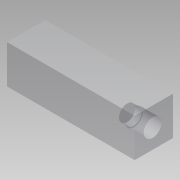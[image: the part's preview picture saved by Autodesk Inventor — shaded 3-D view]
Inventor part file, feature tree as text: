
AUTODESK INVENTOR PART (.ipt)
format: ipt  version: 2014 (Build 180170000, 170)  size: 129,024 bytes
history: native  units: mm
features: other x48, extrude x4, sketch x4
ambient origin geometry x8: Origin, YZ Plane, XZ Plane, XY Plane, X Axis, Y Axis, Z Axis, Center Point
bodies: 实体1 (feature_tree)
feature tree (56):
  extrude  "拉伸1"  Depth=20.0mm
  other  "UCS1"
  other  "UCS2"
  other  "UCS3"
  other  "UCS4"
  other  "UCS5"
  other  "UCS6"
  extrude  "拉伸2"  Depth=20.0mm
  extrude  "拉伸3"  Depth=20.0mm
  extrude  "拉伸4"  Depth=20.0mm TaperAngle=0.0deg
  sketch  "草图1"  dims[d0=30.0mm d1=0.0mm]
  sketch  "草图2"  dims[d2=0.0mm d3=0.0mm d4=0.0mm d5=0.0mm d6=0.0mm d7=0.0mm]
  sketch  "草图3"  dims[d8=0.0mm d9=0.0mm d10=0.0mm d11=0.0mm d12=0.0mm d13=0.0mm]
  sketch  "草图4"  dims[d14=0.0mm d15=0.0mm d16=0.0mm d17=0.0mm d18=0.0mm d19=0.0mm d20=0.0mm d21=0.0mm d22=0.0mm d23=0.0mm d24=0.0mm d25=0.0mm d26=0.0mm d27=0.0mm d28=0.0mm d29=0.0mm d30=0.0mm d31=0.0mm d32=0.0mm d33=0.0mm d34=0.0mm d35=0.0mm d36=0.0mm d37=0.0mm d38=14.0mm d39=15.0mm d40=14.0mm d41=14.5mm d42=0.0mm d43=14.5mm d44=-10.471976mm d45=12.7mm d46=20.0mm d47=0.0mm]
  other  "UCS1: YZ 平面"
  other  "UCS1: XZ 平面"
  other  "UCS1: XY 平面"
  other  "UCS1: X 轴"
  other  "UCS1: Y 轴"
  other  "UCS1: Z 轴"
  other  "UCS1: 原点"
  other  "UCS2: YZ 平面"
  other  "UCS2: XZ 平面"
  other  "UCS2: XY 平面"
  other  "UCS2: X 轴"
  other  "UCS2: Y 轴"
  other  "UCS2: Z 轴"
  other  "UCS2: 原点"
  other  "UCS3: YZ 平面"
  other  "UCS3: XZ 平面"
  other  "UCS3: XY 平面"
  other  "UCS3: X 轴"
  other  "UCS3: Y 轴"
  other  "UCS3: Z 轴"
  other  "UCS3: 原点"
  other  "UCS4: YZ 平面"
  other  "UCS4: XZ 平面"
  other  "UCS4: XY 平面"
  other  "UCS4: X 轴"
  other  "UCS4: Y 轴"
  other  "UCS4: Z 轴"
  other  "UCS4: 原点"
  other  "UCS5: YZ 平面"
  other  "UCS5: XZ 平面"
  other  "UCS5: XY 平面"
  other  "UCS5: X 轴"
  other  "UCS5: Y 轴"
  other  "UCS5: Z 轴"
  other  "UCS5: 原点"
  other  "UCS6: YZ 平面"
  other  "UCS6: XZ 平面"
  other  "UCS6: XY 平面"
  other  "UCS6: X 轴"
  other  "UCS6: Y 轴"
  other  "UCS6: Z 轴"
  other  "UCS6: 原点"
